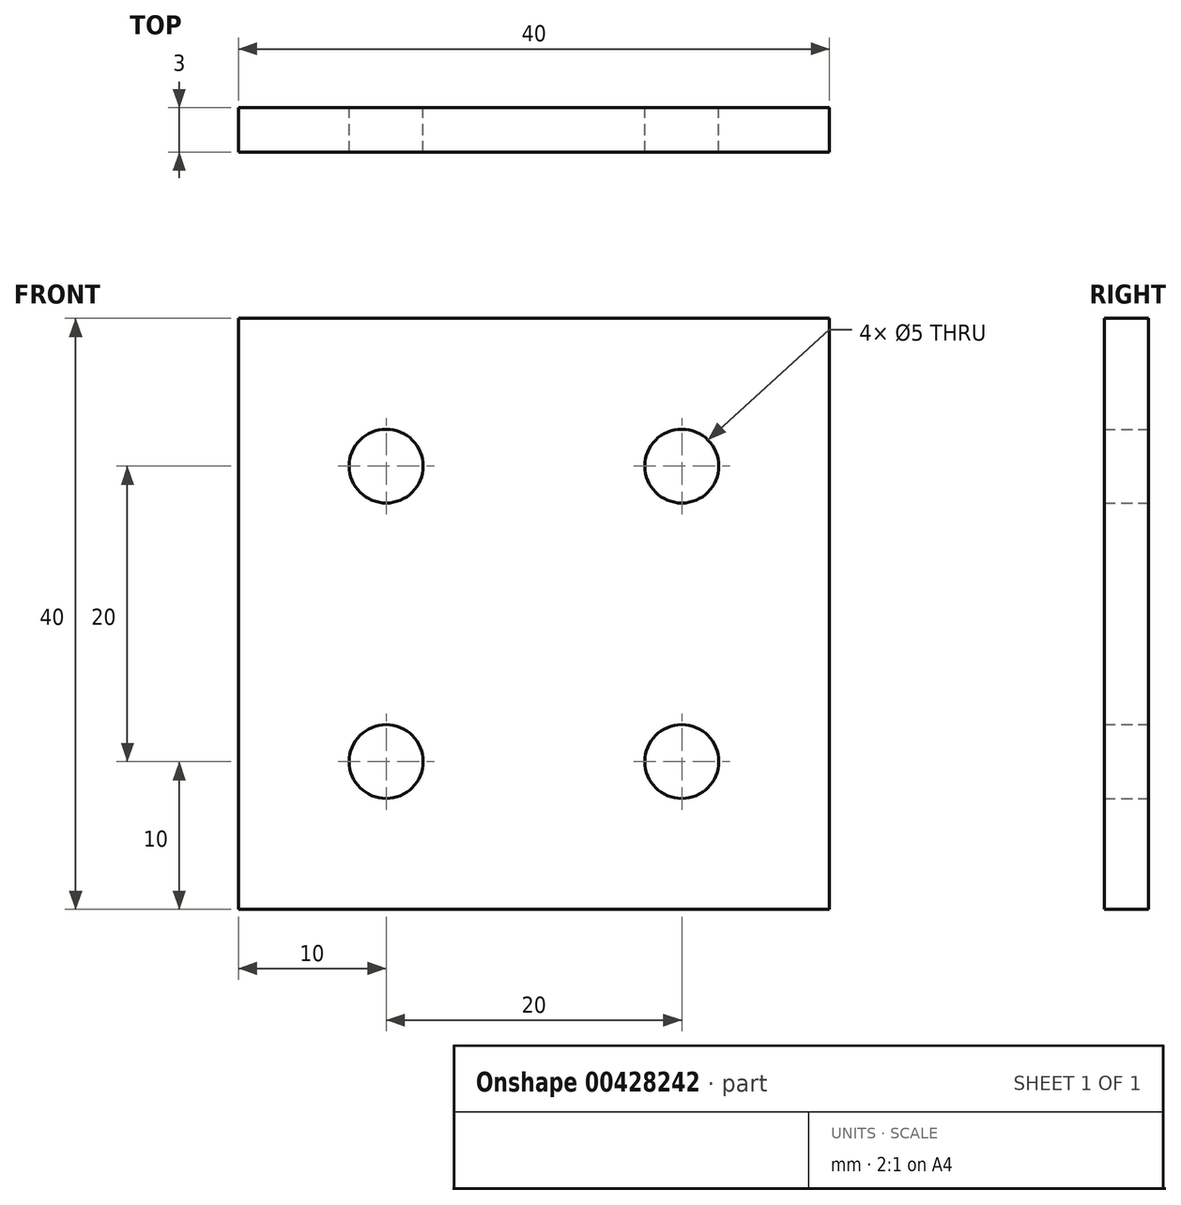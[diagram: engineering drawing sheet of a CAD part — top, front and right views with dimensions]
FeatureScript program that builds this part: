
annotation { "Feature Type Name" : "Feature", "Feature Type Description" : "" }
export const myFeature = defineFeature(function(context is Context, id is Id, definition is map)
    precondition{}
    {
        {
            var Q0;
            Q0=qCreatedBy(makeId("Front.planeOp"),FACE);
            var sketch = newSketch(context, id + "F0", { "sketchPlane" : qUnion([Q0])});
            skCircle(sketch, "E0", {"center": v(-10, -10) * mm, "radius": 2.5 * mm});
            skLineSegment(sketch, "E1.bottom", {"start": v(20, -20) * mm, "end": v(-20, -20) * mm});
            skLineSegment(sketch, "E1.top", {"start": v(20, 20) * mm, "end": v(-20, 20) * mm});
            skLineSegment(sketch, "E1.left", {"start": v(20, -20) * mm, "end": v(20, 20) * mm});
            skLineSegment(sketch, "E1.right", {"start": v(-20, -20) * mm, "end": v(-20, 20) * mm});
            skPoint(sketch, "E1.middle", {"position": v(0, 0) * mm});
            skCircle(sketch, "E2.MirrorC", {"center": v(-10, 10) * mm, "radius": 2.5 * mm});
            skCircle(sketch, "E3.MirrorC", {"center": v(10, 10) * mm, "radius": 2.5 * mm});
            skCircle(sketch, "E4.MirrorC", {"center": v(10, -10) * mm, "radius": 2.5 * mm});
            skSolve(sketch);
        }
        {
            var Q0;
            Q0=makeQuery(id+"F0.imprint","IMPRINT",FACE,{"disambiguationData":[TD([[makeQuery(id+"F0.imprint","IMPRINT",EDGE,{"derivedFrom":sQuery(id+"F0.wireOp",EDGE,"E0")}),-1.0]])]});
            extrude(context, id + "F1", {"entities" : qUnion([Q0]), "depth" : 3 * mm, "offsetDistance" : 25.4 * mm});
        }
    });
